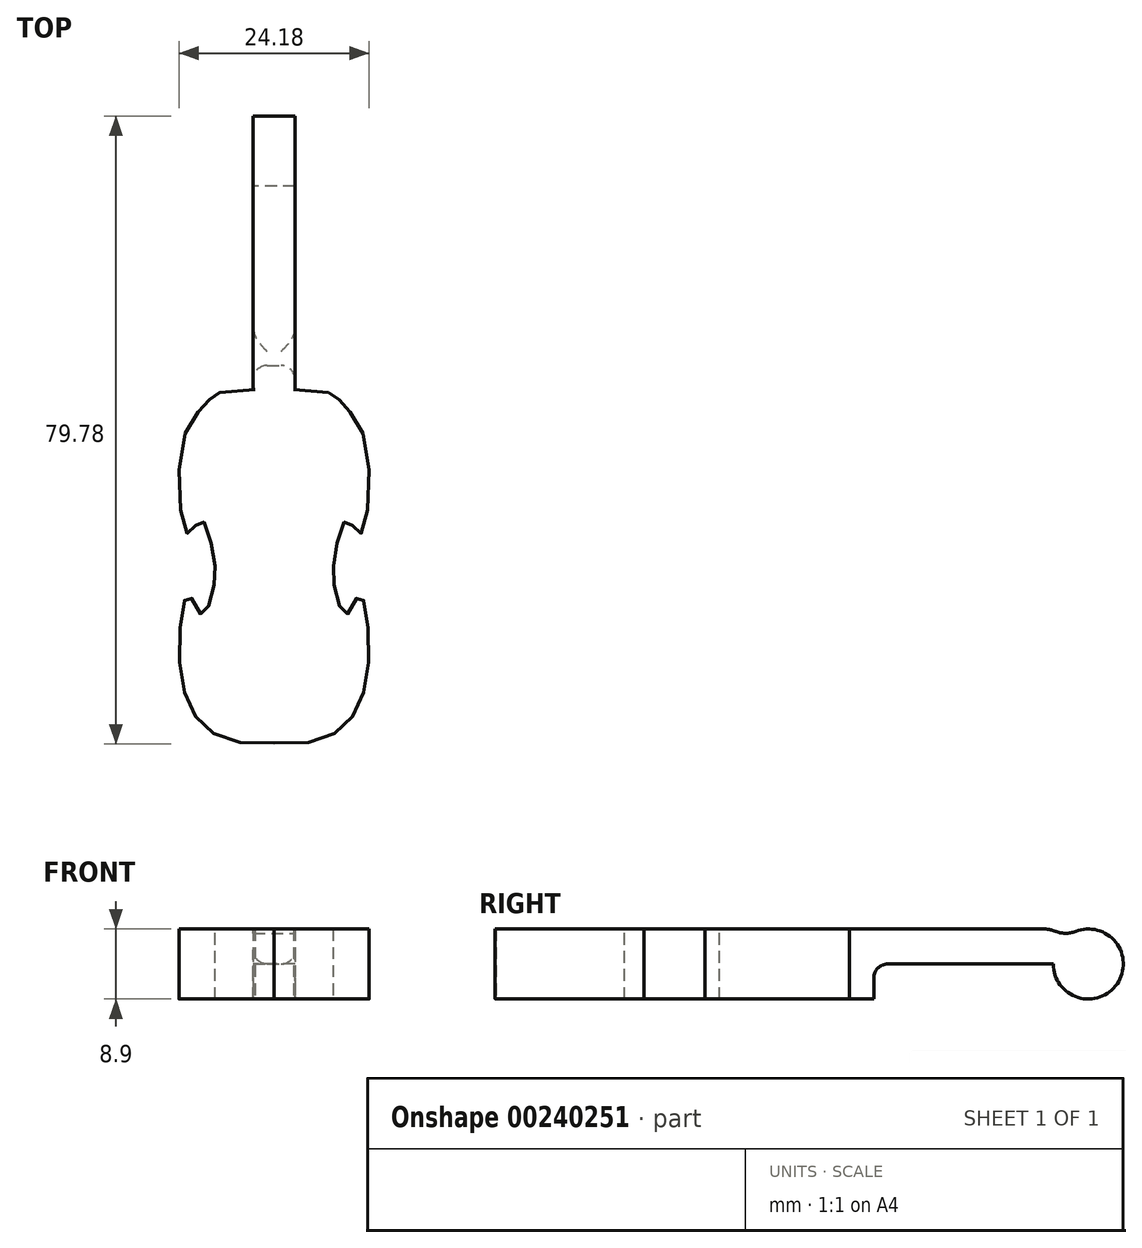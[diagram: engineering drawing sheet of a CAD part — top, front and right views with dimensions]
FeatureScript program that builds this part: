
annotation { "Feature Type Name" : "Feature", "Feature Type Description" : "" }
export const myFeature = defineFeature(function(context is Context, id is Id, definition is map)
    precondition{}
    {
        {
            var Q0;
            Q0=qCreatedBy(makeId("Top.planeOp"),FACE);
            var sketch = newSketch(context, id + "F0", { "sketchPlane" : qUnion([Q0])});
            skFitSpline(sketch, "E0", {"points": [v(0, -34.54) * mm, v(-13.4, -30.75) * mm, v(-17.2, -17.63) * mm, v(-15.45, -7.72) * mm, v(-13.12, -11.22) * mm, v(-11.08, -6.85) * mm, v(-11.08, 0) * mm, v(-13.4, 5.98) * mm, v(-15.45, 3.35) * mm, v(-16.61, 19.97) * mm, v(-11.95, 27.54) * mm, v(-3.5, 29.58) * mm], "startDerivative": vector(-160.37, -17.82) * mm, "endDerivative": vector(238.62, 0) * mm});
            skLineSegment(sketch, "E1", {"start": v(-3.79, 29.58) * mm, "end": v(-3.5, 29.58) * mm});
            skLineSegment(sketch, "E2", {"start": v(-3.79, 29.58) * mm, "end": v(-3.79, 68.64) * mm});
            skLineSegment(sketch, "E3", {"start": v(0, 75.64) * mm, "end": v(0, -76.8) * mm, "construction": true});
            skLineSegment(sketch, "E4.MirrorCS", {"start": v(3.79, 29.58) * mm, "end": v(3.5, 29.58) * mm});
            skFitSpline(sketch, "E5.MirrorCS", {"points": [v(0, -34.54) * mm, v(13.4, -30.75) * mm, v(17.2, -17.63) * mm, v(15.45, -7.72) * mm, v(13.12, -11.22) * mm, v(11.08, -6.85) * mm, v(11.08, 0) * mm, v(13.4, 5.98) * mm, v(15.45, 3.35) * mm, v(16.61, 19.97) * mm, v(11.95, 27.54) * mm, v(3.5, 29.58) * mm], "startDerivative": vector(160.37, -17.82) * mm, "endDerivative": vector(-238.62, 0) * mm});
            skLineSegment(sketch, "E6.MirrorCS", {"start": v(3.79, 29.58) * mm, "end": v(3.79, 68.64) * mm});
            skLineSegment(sketch, "E7", {"start": v(3.79, 68.64) * mm, "end": v(-3.79, 68.64) * mm});
            skSolve(sketch);
        }
        {
            var Q0;
            Q0 = qSketchRegion(id + "F0", true);
            extrude(context, id + "F1", {"entities" : qUnion([Q0]), "endBound" : BoundingType.SYMMETRIC, "depth" : 12.7 * mm});
        }
        {
            var Q0;
            Q0=makeQuery(id+"F1.opExtrude","SWEPT_FACE",FACE,{"disambiguationData":[OSD([sQuery(id+"F0.wireOp",EDGE,"E2")])]});
            var sketch = newSketch(context, id + "F2", { "sketchPlane" : qUnion([Q0])});
            skLineSegment(sketch, "E8", {"start": v(-33.98, -6.35) * mm, "end": v(-33.98, 0) * mm});
            skLineSegment(sketch, "E9", {"start": v(-33.98, 0) * mm, "end": v(-71.64, 0) * mm});
            skLineSegment(sketch, "E10", {"start": v(-71.64, 0) * mm, "end": v(-71.64, -11.75) * mm});
            skLineSegment(sketch, "E11", {"start": v(-71.64, -11.75) * mm, "end": v(-33.98, -6.35) * mm});
            skSolve(sketch);
        }
        {
            var Q0;
            Q0 = qSketchRegion(id + "F2", true);
            extrude(context, id + "F3", {"entities" : qUnion([Q0]), "operationType" : NewBodyOperationType.REMOVE, "endBound" : BoundingType.SYMMETRIC, "depth" : 101.6 * mm});
        }
        {
            var Q0;
            Q0=makeQuery(id+"F3.boolean.opBoolean","INTERSECT",EDGE,{"derivedFrom":[makeQuery(id+"F1.opExtrude","SWEPT_FACE",FACE,{"disambiguationData":[OSD([sQuery(id+"F0.wireOp",EDGE,"E2")])]}),makeQuery(id+"F3.opExtrude","SWEPT_FACE",FACE,{"disambiguationData":[OSD([sQuery(id+"F2.wireOp",EDGE,"E8")])]})]});
            var Q1;
            Q1=makeQuery(id+"F3.boolean.opBoolean","INTERSECT",EDGE,{"derivedFrom":[makeQuery(id+"F1.opExtrude","SWEPT_FACE",FACE,{"disambiguationData":[OSD([sQuery(id+"F0.wireOp",EDGE,"E6.MirrorCS")])]}),makeQuery(id+"F3.opExtrude","SWEPT_FACE",FACE,{"disambiguationData":[OSD([sQuery(id+"F2.wireOp",EDGE,"E8")])]})]});
            var Q2;
            Q2=makeQuery(id+"F3.boolean.opBoolean","COPY",EDGE,{"derivedFrom":makeQuery(id+"F3.opExtrude","SWEPT_EDGE",EDGE,{"disambiguationData":[OSD([sQuery(id+"F2.wireOp",EDGE,"E8"),sQuery(id+"F2.wireOp",EDGE,"E9")])]})});
            fillet(context, id + "F4", {"entities" : qUnion([Q0, Q1, Q2]), "radius" : 2.54 * mm, "tangentPropagation" : true, "allowEdgeOverflow" : false});
        }
        {
            var Q0;
            Q0=makeQuery(id+"F1.opExtrude","SWEPT_FACE",FACE,{"disambiguationData":[OSD([sQuery(id+"F0.wireOp",EDGE,"E2")])]});
            var sketch = newSketch(context, id + "F5", { "sketchPlane" : qUnion([Q0])});
            skCircle(sketch, "E12", {"center": v(-72.91, 0) * mm, "radius": 6.35 * mm});
            skLineSegment(sketch, "E13", {"start": v(-64, 6.35) * mm, "end": v(-87.97, 6.35) * mm, "construction": true});
            skSolve(sketch);
        }
        {
            var Q0;
            Q0 = qSketchRegion(id + "F5", true);
            var Q1;
            Q1=makeQuery(id+"F1.opExtrude","SWEPT_FACE",FACE,{"disambiguationData":[OSD([sQuery(id+"F0.wireOp",EDGE,"E6.MirrorCS")])]});
            extrude(context, id + "F6", {"entities" : qUnion([Q0]), "operationType" : NewBodyOperationType.ADD, "endBound" : BoundingType.UP_TO_SURFACE, "oppositeDirection" : true, "endBoundEntityFace" : qUnion([Q1]), "depth" : 5.3 * mm});
        }
        {
            var Q0;
            Q0=makeQuery(id+"F1.opExtrude","CAP_EDGE",EDGE,{"disambiguationData":[OSD([sQuery(id+"F0.wireOp",EDGE,"E7")])],"isStart":false});
            fillet(context, id + "F7", {"entities" : qUnion([Q0]), "radius" : 5.08 * mm, "tangentPropagation" : true, "allowEdgeOverflow" : false});
        }
        {
            var Q0;
            Q0=makeQuery(id+"F7.opFillet","BLEND_EDGE",EDGE,{"blendedFrom":[makeQuery(id+"F1.opExtrude","CAP_EDGE",EDGE,{"disambiguationData":[OSD([sQuery(id+"F0.wireOp",EDGE,"E7")])],"isStart":false}),makeQuery(id+"F6.opExtrude","SWEPT_FACE",FACE,{"disambiguationData":[OSD([sQuery(id+"F5.wireOp",EDGE,"E12")])]})],"blendedInto":[makeQuery(id+"F6.opExtrude","SWEPT_FACE",FACE,{"disambiguationData":[OSD([sQuery(id+"F5.wireOp",EDGE,"E12")])]})]});
            fillet(context, id + "F8", {"entities" : qUnion([Q0]), "radius" : 5.08 * mm, "tangentPropagation" : true, "allowEdgeOverflow" : false});
        }
        {
            var Q0;
            Q0=makeQuery(id+"F1.opExtrude","SWEPT_BODY",BODY,{"disambiguationData":[OSD([sQuery(id+"F0.wireOp",EDGE,"E0"),sQuery(id+"F0.wireOp",EDGE,"E1"),sQuery(id+"F0.wireOp",EDGE,"E2"),sQuery(id+"F0.wireOp",EDGE,"E4.MirrorCS"),sQuery(id+"F0.wireOp",EDGE,"E5.MirrorCS"),sQuery(id+"F0.wireOp",EDGE,"E6.MirrorCS"),sQuery(id+"F0.wireOp",EDGE,"E7")])]});
            var Q1;
            Q1=qCreatedBy(makeId("Origin.pointOp"),VERTEX);
            transform(context, id + "F9", {"entities" : qUnion([Q0]), "transformType" : TransformType.SCALE_UNIFORMLY, "scale" : .7, "scalePoint" : qUnion([Q1]), "makeCopy" : false});
        }
    });
